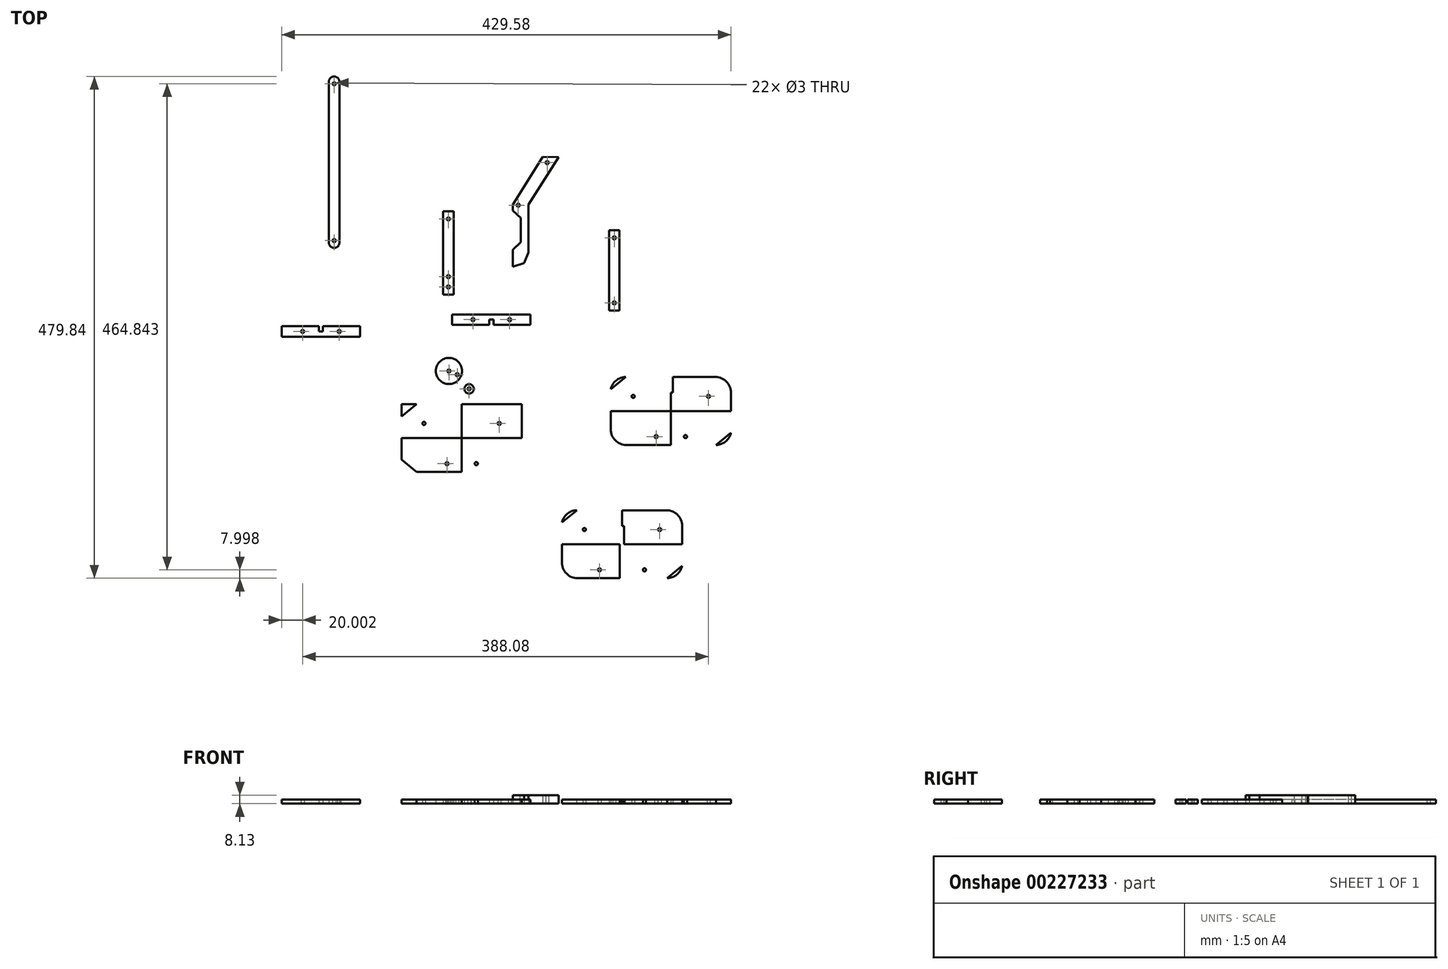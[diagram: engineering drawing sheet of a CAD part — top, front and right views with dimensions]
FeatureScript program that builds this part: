
annotation { "Feature Type Name" : "Feature", "Feature Type Description" : "" }
export const myFeature = defineFeature(function(context is Context, id is Id, definition is map)
    precondition{}
    {
        {
            var Q0;
            Q0=qCreatedBy(makeId("Top.planeOp"),FACE);
            var sketch = newSketch(context, id + "F0", { "sketchPlane" : qUnion([Q0])});
            skLineSegment(sketch, "E0", {"start": v(0, 50.66) * mm, "end": v(0, 45.05) * mm});
            skLineSegment(sketch, "E1", {"start": v(10.8, -5.12) * mm, "end": v(15.08, 4.77) * mm});
            skLineSegment(sketch, "E2", {"start": v(15.08, 4.77) * mm, "end": v(15.08, 50.66) * mm});
            skLineSegment(sketch, "E3", {"start": v(0, -8.6) * mm, "end": v(10.8, -5.12) * mm});
            skLineSegment(sketch, "E4", {"start": v(0, 50.66) * mm, "end": v(28.73, 96.18) * mm});
            skLineSegment(sketch, "E5", {"start": v(15.08, 50.66) * mm, "end": v(43.73, 96.06) * mm});
            skLineSegment(sketch, "E6", {"start": v(43.73, 96.06) * mm, "end": v(28.73, 96.18) * mm});
            skLineSegment(sketch, "E7", {"start": v(25.34, 90.81) * mm, "end": v(40.42, 90.81) * mm});
            skCircle(sketch, "E8", {"center": v(32.88, 90.81) * mm, "radius": 1.5 * mm});
            skLineSegment(sketch, "E9", {"start": v(0, 50.05) * mm, "end": v(15.08, 50.05) * mm});
            skCircle(sketch, "E10", {"center": v(5.2, 50.05) * mm, "radius": 1.5 * mm});
            skLineSegment(sketch, "E11", {"start": v(0, 7.4) * mm, "end": v(0, -8.6) * mm});
            skLineSegment(sketch, "E12", {"start": v(0, 45.05) * mm, "end": v(7.77, 45.05) * mm});
            skLineSegment(sketch, "E13", {"start": v(7.77, 45.05) * mm, "end": v(7.77, 7.4) * mm});
            skLineSegment(sketch, "E14", {"start": v(7.77, 7.4) * mm, "end": v(0, 7.4) * mm});
            skLineSegment(sketch, "E15", {"start": v(7.77, 26.22) * mm, "end": v(-3.47, 26.22) * mm});
            skLineSegment(sketch, "E16", {"start": v(0, 45.05) * mm, "end": v(7.77, 37.82) * mm});
            skLineSegment(sketch, "E17.MirrorCS", {"start": v(0, 7.4) * mm, "end": v(7.77, 14.63) * mm});
            skSolve(sketch);
        }
        {
            var Q0;
            Q0=makeQuery(id+"F0.imprint","IMPRINT",FACE,{"disambiguationData":[TD([[makeQuery(id+"F0.imprint","IMPRINT",EDGE,{"derivedFrom":sQuery(id+"F0.wireOp",EDGE,"xkdn2cEw-GIe6-0bhZ-HK7p-8BZ6EKmmzaHg")}),-1.0]])]});
            var Q1;
            Q1=makeQuery(id+"F0.imprint","IMPRINT",FACE,{"disambiguationData":[TD([[makeQuery(id+"F0.imprint","IMPRINT",EDGE,{"derivedFrom":sQuery(id+"F0.wireOp",EDGE,"E0")}),1.0]])]});
            var Q2;
            {var subQ5=sQuery(id+"F0.wireOp",EDGE,"E6");Q2=makeQuery(id+"F0.imprint","IMPRINT",FACE,{"disambiguationData":[TD([[makeQuery(id+"F0.imprint","IMPRINT",EDGE,{"derivedFrom":subQ5}),1.0]])]});}
            var Q3;
            {var subQ8=sQuery(id+"F0.wireOp",EDGE,"YExFYflc-ZLWd-MDCy-k9qd-3KOZYN6Y7YQf");Q3=makeQuery(id+"F0.imprint","IMPRINT",FACE,{"disambiguationData":[TD([[makeQuery(id+"F0.imprint","IMPRINT",EDGE,{"derivedFrom":subQ8}),1.0]])]});}
            var Q4;
            {var subQ15=sQuery(id+"F0.wireOp",EDGE,"E1");Q4=makeQuery(id+"F0.imprint","IMPRINT",FACE,{"disambiguationData":[TD([[makeQuery(id+"F0.imprint","IMPRINT",EDGE,{"derivedFrom":subQ15}),1.0]])]});}
            var Q5;
            {var subQ0=sQuery(id+"F0.wireOp",EDGE,"X9um9Srh-HxDp-66OW-7rEK-KayJhXlhD1Sx");Q5=makeQuery(id+"F0.imprint","IMPRINT",FACE,{"disambiguationData":[TD([[makeQuery(id+"F0.imprint","IMPRINT",EDGE,{"derivedFrom":subQ0}),-1.0]])]});}
            var Q6;
            {var subQ0=sQuery(id+"F0.wireOp",EDGE,"I0A4r3CH-8MeB-Zr2p-VjG7-bgiyZAQsyFYi");Q6=makeQuery(id+"F0.imprint","IMPRINT",FACE,{"disambiguationData":[TD([[makeQuery(id+"F0.imprint","IMPRINT",EDGE,{"derivedFrom":subQ0}),-1.0]])]});}
            var Q7;
            {var subQ0=sQuery(id+"F0.wireOp",EDGE,"E12");Q7=makeQuery(id+"F0.imprint","IMPRINT",FACE,{"disambiguationData":[TD([[makeQuery(id+"F0.imprint","IMPRINT",EDGE,{"derivedFrom":subQ0}),-1.0]])]});}
            var Q8;
            {var subQ0=sQuery(id+"F0.wireOp",EDGE,"E14");Q8=makeQuery(id+"F0.imprint","IMPRINT",FACE,{"disambiguationData":[TD([[makeQuery(id+"F0.imprint","IMPRINT",EDGE,{"derivedFrom":subQ0}),-1.0]])]});}
            extrude(context, id + "F1", {"entities" : qUnion([Q0, Q1, Q2, Q3, Q4, Q5, Q6, Q7, Q8]), "depth" : 8.13 * mm});
        }
        {
            var Q0;
            Q0=qCreatedBy(makeId("Top.planeOp"),FACE);
            var sketch = newSketch(context, id + "F2", { "sketchPlane" : qUnion([Q0])});
            skLineSegment(sketch, "E18.bottom", {"start": v(-66.59, 44.42) * mm, "end": v(-56.59, 44.42) * mm});
            skLineSegment(sketch, "E18.top", {"start": v(-66.59, -35.58) * mm, "end": v(-56.59, -35.58) * mm});
            skLineSegment(sketch, "E18.left", {"start": v(-66.59, 44.42) * mm, "end": v(-66.59, -35.58) * mm});
            skLineSegment(sketch, "E18.right", {"start": v(-56.59, 44.42) * mm, "end": v(-56.59, -35.58) * mm});
            skCircle(sketch, "E19", {"center": v(-61.59, -28.08) * mm, "radius": 1.5 * mm});
            skPoint(sketch, "E19.centerSnap0", {"position": v(-61.59, -35.58) * mm});
            skCircle(sketch, "E20", {"center": v(-61.59, 36.92) * mm, "radius": 1.5 * mm});
            skPoint(sketch, "E20.centerSnap0", {"position": v(-61.59, 44.42) * mm});
            skLineSegment(sketch, "E21.bottom", {"start": v(-106.43, -140.09) * mm, "end": v(8.57, -140.09) * mm});
            skLineSegment(sketch, "E21.top", {"start": v(-106.43, -205.09) * mm, "end": v(8.57, -205.09) * mm});
            skLineSegment(sketch, "E21.left", {"start": v(-106.43, -140.09) * mm, "end": v(-106.43, -205.09) * mm});
            skLineSegment(sketch, "E21.right", {"start": v(8.57, -140.09) * mm, "end": v(8.57, -205.09) * mm});
            skCircle(sketch, "E22", {"center": v(-62.93, -197.09) * mm, "radius": 1.5 * mm});
            skCircle(sketch, "E23", {"center": v(-12.93, -158.59) * mm, "radius": 1.5 * mm});
            skCircle(sketch, "E24", {"center": v(-61.08, -108.47) * mm, "radius": 12.5 * mm});
            skCircle(sketch, "E25", {"center": v(-61.08, -108.47) * mm, "radius": 1.5 * mm});
            skCircle(sketch, "E26", {"center": v(-53.14, -111.96) * mm, "radius": 1.5 * mm});
            skLineSegment(sketch, "E27.bottom", {"start": v(92.03, 18.82) * mm, "end": v(102.03, 18.82) * mm});
            skLineSegment(sketch, "E27.top", {"start": v(92.03, -43.35) * mm, "end": v(102.03, -43.35) * mm});
            skLineSegment(sketch, "E27.left", {"start": v(92.03, 18.82) * mm, "end": v(92.03, -43.35) * mm});
            skLineSegment(sketch, "E27.right", {"start": v(102.03, 18.82) * mm, "end": v(102.03, -43.35) * mm});
            skCircle(sketch, "E28", {"center": v(97.03, -43.35) * mm, "radius": 1.5 * mm});
            skCircle(sketch, "E29", {"center": v(97.03, 18.82) * mm, "radius": 1.5 * mm});
            skLineSegment(sketch, "E30", {"start": v(92.03, 18.82) * mm, "end": v(92.03, 26.3) * mm});
            skLineSegment(sketch, "E31", {"start": v(92.03, 26.3) * mm, "end": v(102.03, 26.3) * mm});
            skLineSegment(sketch, "E32", {"start": v(102.03, 26.3) * mm, "end": v(102.03, 18.82) * mm});
            skLineSegment(sketch, "E33", {"start": v(92.03, -43.35) * mm, "end": v(92.03, -50.57) * mm});
            skLineSegment(sketch, "E34", {"start": v(92.03, -50.57) * mm, "end": v(102.03, -50.57) * mm});
            skLineSegment(sketch, "E35", {"start": v(102.03, -50.57) * mm, "end": v(102.03, -43.35) * mm});
            skCircle(sketch, "E36", {"center": v(-41.76, -125.54) * mm, "radius": 4.5 * mm});
            skCircle(sketch, "E37", {"center": v(-41.76, -125.54) * mm, "radius": 1.5 * mm});
            skLineSegment(sketch, "E38", {"start": v(-48.93, -205.09) * mm, "end": v(-48.93, -140.09) * mm});
            skCircle(sketch, "E39.MirrorC", {"center": v(-84.93, -158.59) * mm, "radius": 1.5 * mm});
            skCircle(sketch, "E40.MirrorC", {"center": v(-34.93, -197.09) * mm, "radius": 1.5 * mm});
            skLineSegment(sketch, "E41", {"start": v(-106.43, -151.83) * mm, "end": v(-92.1, -140.09) * mm});
            skLineSegment(sketch, "E42", {"start": v(-106.43, -172.59) * mm, "end": v(8.57, -172.59) * mm});
            skLineSegment(sketch, "E43.MirrorCS", {"start": v(8.57, -151.83) * mm, "end": v(-5.75, -140.09) * mm});
            skLineSegment(sketch, "E44.MirrorCS", {"start": v(8.57, -193.35) * mm, "end": v(-5.75, -205.09) * mm});
            skLineSegment(sketch, "E45.MirrorCS", {"start": v(-106.43, -193.35) * mm, "end": v(-92.1, -205.09) * mm});
            skLineSegment(sketch, "E46", {"start": v(-66.59, -18.19) * mm, "end": v(-56.59, -18.19) * mm});
            skCircle(sketch, "E47", {"center": v(-61.59, -18.19) * mm, "radius": 1.5 * mm});
            skLineSegment(sketch, "E48.bottom", {"start": v(-58.07, -54.39) * mm, "end": v(16.93, -54.39) * mm});
            skLineSegment(sketch, "E48.top", {"start": v(-58.07, -64.39) * mm, "end": v(16.93, -64.39) * mm});
            skLineSegment(sketch, "E48.left", {"start": v(-58.07, -54.39) * mm, "end": v(-58.07, -64.39) * mm});
            skLineSegment(sketch, "E48.right", {"start": v(16.93, -54.39) * mm, "end": v(16.93, -64.39) * mm});
            skLineSegment(sketch, "E49", {"start": v(-38.07, -54.39) * mm, "end": v(-38.07, -64.39) * mm});
            skLineSegment(sketch, "E50", {"start": v(-3.07, -54.39) * mm, "end": v(-3.07, -64.39) * mm});
            skCircle(sketch, "E51", {"center": v(-38.07, -59.39) * mm, "radius": 1.5 * mm});
            skCircle(sketch, "E52", {"center": v(-3.07, -59.39) * mm, "radius": 1.5 * mm});
            skLineSegment(sketch, "E53.bottom", {"start": v(-175.82, 166.2) * mm, "end": v(-165.82, 166.2) * mm});
            skLineSegment(sketch, "E53.top", {"start": v(-175.82, 16.2) * mm, "end": v(-165.82, 16.2) * mm});
            skLineSegment(sketch, "E53.left", {"start": v(-175.82, 166.2) * mm, "end": v(-175.82, 16.2) * mm});
            skLineSegment(sketch, "E53.right", {"start": v(-165.82, 166.2) * mm, "end": v(-165.82, 16.2) * mm});
            skCircle(sketch, "E54", {"center": v(-170.82, 166.2) * mm, "radius": 1.5 * mm});
            skCircle(sketch, "E55", {"center": v(-170.82, 16.2) * mm, "radius": 1.5 * mm});
            skLineSegment(sketch, "E56", {"start": v(-175.82, 166.2) * mm, "end": v(-175.82, 173.2) * mm});
            skLineSegment(sketch, "E57", {"start": v(-175.82, 173.2) * mm, "end": v(-165.82, 173.2) * mm});
            skLineSegment(sketch, "E58", {"start": v(-165.82, 173.2) * mm, "end": v(-165.82, 166.2) * mm});
            skLineSegment(sketch, "E59", {"start": v(-175.82, 16.2) * mm, "end": v(-175.82, 9.2) * mm});
            skLineSegment(sketch, "E60", {"start": v(-175.82, 9.2) * mm, "end": v(-165.82, 9.2) * mm});
            skLineSegment(sketch, "E61", {"start": v(-165.82, 9.2) * mm, "end": v(-165.82, 16.2) * mm});
            skLineSegment(sketch, "E62.bottom", {"start": v(93.6, -114.22) * mm, "end": v(208.6, -114.22) * mm});
            skLineSegment(sketch, "E62.top", {"start": v(93.6, -179.22) * mm, "end": v(208.6, -179.22) * mm});
            skLineSegment(sketch, "E62.left", {"start": v(93.6, -114.22) * mm, "end": v(93.6, -179.22) * mm});
            skLineSegment(sketch, "E62.right", {"start": v(208.6, -114.22) * mm, "end": v(208.6, -179.22) * mm});
            skCircle(sketch, "E63", {"center": v(137.1, -171.22) * mm, "radius": 1.5 * mm});
            skCircle(sketch, "E64", {"center": v(187.1, -132.72) * mm, "radius": 1.5 * mm});
            skLineSegment(sketch, "E65", {"start": v(151.1, -179.22) * mm, "end": v(151.1, -114.22) * mm});
            skCircle(sketch, "E66.MirrorC", {"center": v(115.1, -132.72) * mm, "radius": 1.5 * mm});
            skCircle(sketch, "E67.MirrorC", {"center": v(165.1, -171.22) * mm, "radius": 1.5 * mm});
            skLineSegment(sketch, "E68", {"start": v(93.6, -125.96) * mm, "end": v(107.91, -114.22) * mm});
            skLineSegment(sketch, "E69", {"start": v(93.6, -146.72) * mm, "end": v(208.6, -146.72) * mm});
            skLineSegment(sketch, "E70.MirrorCS", {"start": v(208.6, -125.96) * mm, "end": v(194.27, -114.22) * mm});
            skLineSegment(sketch, "E71.MirrorCS", {"start": v(208.6, -167.48) * mm, "end": v(194.27, -179.22) * mm});
            skLineSegment(sketch, "E72.MirrorCS", {"start": v(93.6, -167.48) * mm, "end": v(107.91, -179.22) * mm});
            skLineSegment(sketch, "E73.bottom", {"start": v(46.9, -241.64) * mm, "end": v(161.9, -241.64) * mm});
            skLineSegment(sketch, "E73.top", {"start": v(46.9, -306.64) * mm, "end": v(161.9, -306.64) * mm});
            skLineSegment(sketch, "E73.left", {"start": v(46.9, -241.64) * mm, "end": v(46.9, -306.64) * mm});
            skLineSegment(sketch, "E73.right", {"start": v(161.9, -241.64) * mm, "end": v(161.9, -306.64) * mm});
            skCircle(sketch, "E74", {"center": v(82.9, -298.64) * mm, "radius": 1.5 * mm});
            skCircle(sketch, "E75", {"center": v(140.4, -260.14) * mm, "radius": 1.5 * mm});
            skLineSegment(sketch, "E76", {"start": v(104.4, -306.64) * mm, "end": v(104.4, -241.64) * mm});
            skCircle(sketch, "E77.MirrorC", {"center": v(68.4, -260.14) * mm, "radius": 1.5 * mm});
            skCircle(sketch, "E78.MirrorC", {"center": v(125.9, -298.64) * mm, "radius": 1.5 * mm});
            skLineSegment(sketch, "E79", {"start": v(46.9, -253.38) * mm, "end": v(61.23, -241.64) * mm});
            skLineSegment(sketch, "E80", {"start": v(46.9, -274.14) * mm, "end": v(161.9, -274.14) * mm});
            skLineSegment(sketch, "E81.MirrorCS", {"start": v(161.9, -253.38) * mm, "end": v(147.58, -241.64) * mm});
            skLineSegment(sketch, "E82.MirrorCS", {"start": v(161.9, -294.9) * mm, "end": v(147.58, -306.64) * mm});
            skLineSegment(sketch, "E83.MirrorCS", {"start": v(46.9, -294.9) * mm, "end": v(61.23, -306.64) * mm});
            skLineSegment(sketch, "E84", {"start": v(149.06, -114.22) * mm, "end": v(149.06, -129.22) * mm});
            skLineSegment(sketch, "E85", {"start": v(149.06, -129.22) * mm, "end": v(151.1, -129.22) * mm});
            skLineSegment(sketch, "E86.MirrorCS", {"start": v(153.12, -114.22) * mm, "end": v(153.12, -129.22) * mm});
            skLineSegment(sketch, "E87.MirrorCS", {"start": v(153.12, -129.22) * mm, "end": v(151.1, -129.22) * mm});
            skLineSegment(sketch, "E88", {"start": v(102.37, -306.64) * mm, "end": v(102.37, -256.64) * mm});
            skLineSegment(sketch, "E89", {"start": v(102.37, -256.64) * mm, "end": v(104.4, -256.64) * mm});
            skLineSegment(sketch, "E90.MirrorCS", {"start": v(106.44, -256.64) * mm, "end": v(104.4, -256.64) * mm});
            skLineSegment(sketch, "E91.MirrorCS", {"start": v(106.44, -306.64) * mm, "end": v(106.44, -256.64) * mm});
            skLineSegment(sketch, "E92.bottom", {"start": v(-220.99, -65.64) * mm, "end": v(-145.99, -65.64) * mm});
            skLineSegment(sketch, "E92.top", {"start": v(-220.99, -75.64) * mm, "end": v(-145.99, -75.64) * mm});
            skLineSegment(sketch, "E92.left", {"start": v(-220.99, -65.64) * mm, "end": v(-220.99, -75.64) * mm});
            skLineSegment(sketch, "E92.right", {"start": v(-145.99, -65.64) * mm, "end": v(-145.99, -75.64) * mm});
            skLineSegment(sketch, "E93", {"start": v(-200.99, -65.64) * mm, "end": v(-200.99, -75.64) * mm});
            skLineSegment(sketch, "E94", {"start": v(-165.99, -65.64) * mm, "end": v(-165.99, -75.64) * mm});
            skCircle(sketch, "E95", {"center": v(-200.99, -70.64) * mm, "radius": 1.5 * mm});
            skCircle(sketch, "E96", {"center": v(-165.99, -70.64) * mm, "radius": 1.5 * mm});
            skLineSegment(sketch, "E97", {"start": v(-183.49, -65.64) * mm, "end": v(-183.49, -75.64) * mm});
            skLineSegment(sketch, "E98", {"start": v(-185.52, -65.64) * mm, "end": v(-185.52, -70.64) * mm});
            skLineSegment(sketch, "E99", {"start": v(-185.52, -70.64) * mm, "end": v(-183.49, -70.64) * mm});
            skLineSegment(sketch, "E100.MirrorCS", {"start": v(-181.46, -65.64) * mm, "end": v(-181.46, -70.64) * mm});
            skLineSegment(sketch, "E101.MirrorCS", {"start": v(-181.46, -70.64) * mm, "end": v(-183.49, -70.64) * mm});
            skLineSegment(sketch, "E102", {"start": v(-20.57, -64.39) * mm, "end": v(-20.57, -54.39) * mm});
            skLineSegment(sketch, "E103", {"start": v(-22.6, -64.39) * mm, "end": v(-22.6, -59.39) * mm});
            skLineSegment(sketch, "E104", {"start": v(-22.6, -59.39) * mm, "end": v(-20.57, -59.39) * mm});
            skLineSegment(sketch, "E105.MirrorCS", {"start": v(-18.54, -59.39) * mm, "end": v(-20.57, -59.39) * mm});
            skLineSegment(sketch, "E106.MirrorCS", {"start": v(-18.54, -64.39) * mm, "end": v(-18.54, -59.39) * mm});
            skSolve(sketch);
        }
        {
            var Q0;
            {var subQ3=sQuery(id+"F2.wireOp",EDGE,"E41");Q0=makeQuery(id+"F2.imprint","IMPRINT",FACE,{"disambiguationData":[TD([[makeQuery(id+"F2.imprint","IMPRINT",EDGE,{"derivedFrom":subQ3}),1.0]])]});}
            var Q1;
            Q1=makeQuery(id+"F2.imprint","IMPRINT",FACE,{"disambiguationData":[TD([[makeQuery(id+"F2.imprint","IMPRINT",EDGE,{"derivedFrom":sQuery(id+"F2.wireOp",EDGE,"E18.bottom")}),-1.0]])]});
            var Q2;
            {var subQ3=sQuery(id+"F2.wireOp",EDGE,"E43.MirrorCS");Q2=makeQuery(id+"F2.imprint","IMPRINT",FACE,{"disambiguationData":[TD([[makeQuery(id+"F2.imprint","IMPRINT",EDGE,{"derivedFrom":subQ3}),-1.0]])]});}
            var Q3;
            Q3=makeQuery(id+"F2.imprint","IMPRINT",FACE,{"disambiguationData":[TD([[makeQuery(id+"F2.imprint","IMPRINT",EDGE,{"derivedFrom":sQuery(id+"F2.wireOp",EDGE,"E24")}),1.0]])]});
            var Q4;
            {var subQ4=sQuery(id+"F2.wireOp",EDGE,"E27.left");Q4=makeQuery(id+"F2.imprint","IMPRINT",FACE,{"disambiguationData":[TD([[makeQuery(id+"F2.imprint","IMPRINT",EDGE,{"derivedFrom":subQ4}),1.0]])]});}
            var Q5;
            {var subQ0=sQuery(id+"F2.wireOp",EDGE,"E30");Q5=makeQuery(id+"F2.imprint","IMPRINT",FACE,{"disambiguationData":[TD([[makeQuery(id+"F2.imprint","IMPRINT",EDGE,{"derivedFrom":subQ0}),-1.0]])]});}
            var Q6;
            {var subQ4=sQuery(id+"F2.wireOp",EDGE,"E33");Q6=makeQuery(id+"F2.imprint","IMPRINT",FACE,{"disambiguationData":[TD([[makeQuery(id+"F2.imprint","IMPRINT",EDGE,{"derivedFrom":subQ4}),1.0]])]});}
            var Q7;
            Q7=makeQuery(id+"F2.imprint","IMPRINT",FACE,{"disambiguationData":[TD([[makeQuery(id+"F2.imprint","IMPRINT",EDGE,{"derivedFrom":sQuery(id+"F2.wireOp",EDGE,"E36")}),1.0]])]});
            var Q8;
            Q8=makeQuery(id+"F2.imprint","IMPRINT",FACE,{"disambiguationData":[TD([[makeQuery(id+"F2.imprint","IMPRINT",EDGE,{"derivedFrom":sQuery(id+"F2.wireOp",EDGE,"E39.MirrorC")}),1.0]])]});
            var Q9;
            Q9=makeQuery(id+"F2.imprint","IMPRINT",FACE,{"disambiguationData":[TD([[makeQuery(id+"F2.imprint","IMPRINT",EDGE,{"derivedFrom":sQuery(id+"F2.wireOp",EDGE,"E22")}),-1.0]])]});
            var Q10;
            Q10=makeQuery(id+"F2.imprint","IMPRINT",FACE,{"disambiguationData":[TD([[makeQuery(id+"F2.imprint","IMPRINT",EDGE,{"derivedFrom":sQuery(id+"F2.wireOp",EDGE,"E23")}),-1.0]])]});
            var Q11;
            Q11=makeQuery(id+"F2.imprint","IMPRINT",FACE,{"disambiguationData":[TD([[makeQuery(id+"F2.imprint","IMPRINT",EDGE,{"derivedFrom":sQuery(id+"F2.wireOp",EDGE,"E40.MirrorC")}),1.0]])]});
            var Q12;
            {var subQ1=sQuery(id+"F2.wireOp",EDGE,"E18.top");Q12=makeQuery(id+"F2.imprint","IMPRINT",FACE,{"disambiguationData":[TD([[makeQuery(id+"F2.imprint","IMPRINT",EDGE,{"derivedFrom":subQ1}),1.0]])]});}
            var Q13;
            {var subQ0=sQuery(id+"F2.wireOp",EDGE,"E49");var subQ11=sQuery(id+"F2.wireOp",EDGE,"E48.bottom");var subQ12=makeQuery(id+"F2.imprint","INTERSECT",VERTEX,{"derivedFrom":[subQ11,subQ0]});Q13=makeQuery(id+"F2.imprint","IMPRINT",FACE,{"disambiguationData":[TD([[makeQuery(id+"F2.imprint","IMPRINT",EDGE,{"disambiguationData":[TD([[subQ12,-1.0]])],"derivedFrom":subQ11}),-1.0]])]});}
            var Q14;
            {var subQ0=sQuery(id+"F2.wireOp",EDGE,"E48.left");Q14=makeQuery(id+"F2.imprint","IMPRINT",FACE,{"disambiguationData":[TD([[makeQuery(id+"F2.imprint","IMPRINT",EDGE,{"derivedFrom":subQ0}),1.0]])]});}
            var Q15;
            {var subQ0=sQuery(id+"F2.wireOp",EDGE,"E48.right");Q15=makeQuery(id+"F2.imprint","IMPRINT",FACE,{"disambiguationData":[TD([[makeQuery(id+"F2.imprint","IMPRINT",EDGE,{"derivedFrom":subQ0}),-1.0]])]});}
            var Q16;
            {var subQ5=sQuery(id+"F2.wireOp",EDGE,"E53.left");Q16=makeQuery(id+"F2.imprint","IMPRINT",FACE,{"disambiguationData":[TD([[makeQuery(id+"F2.imprint","IMPRINT",EDGE,{"derivedFrom":subQ5}),1.0]])]});}
            var Q17;
            {var subQ5=sQuery(id+"F2.wireOp",EDGE,"E56");Q17=makeQuery(id+"F2.imprint","IMPRINT",FACE,{"disambiguationData":[TD([[makeQuery(id+"F2.imprint","IMPRINT",EDGE,{"derivedFrom":subQ5}),-1.0]])]});}
            var Q18;
            {var subQ0=sQuery(id+"F2.wireOp",EDGE,"E59");Q18=makeQuery(id+"F2.imprint","IMPRINT",FACE,{"disambiguationData":[TD([[makeQuery(id+"F2.imprint","IMPRINT",EDGE,{"derivedFrom":subQ0}),1.0]])]});}
            var Q19;
            Q19=makeQuery(id+"F2.imprint","IMPRINT",FACE,{"disambiguationData":[TD([[makeQuery(id+"F2.imprint","IMPRINT",EDGE,{"derivedFrom":sQuery(id+"F2.wireOp",EDGE,"E66.MirrorC")}),1.0]])]});
            var Q20;
            Q20=makeQuery(id+"F2.imprint","IMPRINT",FACE,{"disambiguationData":[TD([[makeQuery(id+"F2.imprint","IMPRINT",EDGE,{"derivedFrom":sQuery(id+"F2.wireOp",EDGE,"E63")}),-1.0]])]});
            var Q21;
            Q21=makeQuery(id+"F2.imprint","IMPRINT",FACE,{"disambiguationData":[TD([[makeQuery(id+"F2.imprint","IMPRINT",EDGE,{"derivedFrom":sQuery(id+"F2.wireOp",EDGE,"E67.MirrorC")}),1.0]])]});
            var Q22;
            Q22=makeQuery(id+"F2.imprint","IMPRINT",FACE,{"disambiguationData":[TD([[makeQuery(id+"F2.imprint","IMPRINT",EDGE,{"derivedFrom":sQuery(id+"F2.wireOp",EDGE,"E64")}),-1.0]])]});
            var Q23;
            {var subQ3=sQuery(id+"F2.wireOp",EDGE,"E70.MirrorCS");Q23=makeQuery(id+"F2.imprint","IMPRINT",FACE,{"disambiguationData":[TD([[makeQuery(id+"F2.imprint","IMPRINT",EDGE,{"derivedFrom":subQ3}),-1.0]])]});}
            var Q24;
            {var subQ3=sQuery(id+"F2.wireOp",EDGE,"E68");Q24=makeQuery(id+"F2.imprint","IMPRINT",FACE,{"disambiguationData":[TD([[makeQuery(id+"F2.imprint","IMPRINT",EDGE,{"derivedFrom":subQ3}),1.0]])]});}
            var Q25;
            {var subQ3=sQuery(id+"F2.wireOp",EDGE,"E72.MirrorCS");Q25=makeQuery(id+"F2.imprint","IMPRINT",FACE,{"disambiguationData":[TD([[makeQuery(id+"F2.imprint","IMPRINT",EDGE,{"derivedFrom":subQ3}),-1.0]])]});}
            var Q26;
            {var subQ3=sQuery(id+"F2.wireOp",EDGE,"E71.MirrorCS");Q26=makeQuery(id+"F2.imprint","IMPRINT",FACE,{"disambiguationData":[TD([[makeQuery(id+"F2.imprint","IMPRINT",EDGE,{"derivedFrom":subQ3}),1.0]])]});}
            var Q27;
            Q27=makeQuery(id+"F2.imprint","IMPRINT",FACE,{"disambiguationData":[TD([[makeQuery(id+"F2.imprint","IMPRINT",EDGE,{"derivedFrom":sQuery(id+"F2.wireOp",EDGE,"E78.MirrorC")}),1.0]])]});
            var Q28;
            Q28=makeQuery(id+"F2.imprint","IMPRINT",FACE,{"disambiguationData":[TD([[makeQuery(id+"F2.imprint","IMPRINT",EDGE,{"derivedFrom":sQuery(id+"F2.wireOp",EDGE,"E75")}),-1.0]])]});
            var Q29;
            {var subQ3=sQuery(id+"F2.wireOp",EDGE,"E81.MirrorCS");Q29=makeQuery(id+"F2.imprint","IMPRINT",FACE,{"disambiguationData":[TD([[makeQuery(id+"F2.imprint","IMPRINT",EDGE,{"derivedFrom":subQ3}),-1.0]])]});}
            var Q30;
            {var subQ3=sQuery(id+"F2.wireOp",EDGE,"E82.MirrorCS");Q30=makeQuery(id+"F2.imprint","IMPRINT",FACE,{"disambiguationData":[TD([[makeQuery(id+"F2.imprint","IMPRINT",EDGE,{"derivedFrom":subQ3}),1.0]])]});}
            var Q31;
            Q31=makeQuery(id+"F2.imprint","IMPRINT",FACE,{"disambiguationData":[TD([[makeQuery(id+"F2.imprint","IMPRINT",EDGE,{"derivedFrom":sQuery(id+"F2.wireOp",EDGE,"E74")}),-1.0]])]});
            var Q32;
            {var subQ3=sQuery(id+"F2.wireOp",EDGE,"E83.MirrorCS");Q32=makeQuery(id+"F2.imprint","IMPRINT",FACE,{"disambiguationData":[TD([[makeQuery(id+"F2.imprint","IMPRINT",EDGE,{"derivedFrom":subQ3}),-1.0]])]});}
            var Q33;
            Q33=makeQuery(id+"F2.imprint","IMPRINT",FACE,{"disambiguationData":[TD([[makeQuery(id+"F2.imprint","IMPRINT",EDGE,{"derivedFrom":sQuery(id+"F2.wireOp",EDGE,"E77.MirrorC")}),1.0]])]});
            var Q34;
            {var subQ3=sQuery(id+"F2.wireOp",EDGE,"E79");Q34=makeQuery(id+"F2.imprint","IMPRINT",FACE,{"disambiguationData":[TD([[makeQuery(id+"F2.imprint","IMPRINT",EDGE,{"derivedFrom":subQ3}),1.0]])]});}
            var Q35;
            {var subQ5=sQuery(id+"F2.wireOp",EDGE,"E92.left");Q35=makeQuery(id+"F2.imprint","IMPRINT",FACE,{"disambiguationData":[TD([[makeQuery(id+"F2.imprint","IMPRINT",EDGE,{"derivedFrom":subQ5}),1.0]])]});}
            var Q36;
            {var subQ9=sQuery(id+"F2.wireOp",EDGE,"E98");Q36=makeQuery(id+"F2.imprint","IMPRINT",FACE,{"disambiguationData":[TD([[makeQuery(id+"F2.imprint","IMPRINT",EDGE,{"derivedFrom":subQ9}),-1.0]])]});}
            var Q37;
            {var subQ8=sQuery(id+"F2.wireOp",EDGE,"E100.MirrorCS");Q37=makeQuery(id+"F2.imprint","IMPRINT",FACE,{"disambiguationData":[TD([[makeQuery(id+"F2.imprint","IMPRINT",EDGE,{"derivedFrom":subQ8}),1.0]])]});}
            var Q38;
            {var subQ0=sQuery(id+"F2.wireOp",EDGE,"E92.right");Q38=makeQuery(id+"F2.imprint","IMPRINT",FACE,{"disambiguationData":[TD([[makeQuery(id+"F2.imprint","IMPRINT",EDGE,{"derivedFrom":subQ0}),-1.0]])]});}
            var Q39;
            {var subQ11=sQuery(id+"F2.wireOp",EDGE,"E105.MirrorCS");Q39=makeQuery(id+"F2.imprint","IMPRINT",FACE,{"disambiguationData":[TD([[makeQuery(id+"F2.imprint","IMPRINT",EDGE,{"derivedFrom":subQ11}),-1.0]])]});}
            extrude(context, id + "F3", {"entities" : qUnion([Q0, Q1, Q2, Q3, Q4, Q5, Q6, Q7, Q8, Q9, Q10, Q11, Q12, Q13, Q14, Q15, Q16, Q17, Q18, Q19, Q20, Q21, Q22, Q23, Q24, Q25, Q26, Q27, Q28, Q29, Q30, Q31, Q32, Q33, Q34, Q35, Q36, Q37, Q38, Q39]), "depth" : 4.06 * mm});
        }
        {
            var Q0;
            Q0=makeQuery(id+"F3.opExtrude","SWEPT_EDGE",EDGE,{"disambiguationData":[OSD([sQuery(id+"F2.wireOp",EDGE,"E60"),sQuery(id+"F2.wireOp",EDGE,"E61")])]});
            var Q1;
            Q1=makeQuery(id+"F3.opExtrude","SWEPT_EDGE",EDGE,{"disambiguationData":[OSD([sQuery(id+"F2.wireOp",EDGE,"E59"),sQuery(id+"F2.wireOp",EDGE,"E60")])]});
            fillet(context, id + "F4", {"entities" : qUnion([Q0, Q1]), "radius" : 5 * mm, "tangentPropagation" : true, "allowEdgeOverflow" : false});
        }
        {
            var Q0;
            Q0=makeQuery(id+"F3.opExtrude","SWEPT_EDGE",EDGE,{"disambiguationData":[OSD([sQuery(id+"F2.wireOp",EDGE,"E57"),sQuery(id+"F2.wireOp",EDGE,"E58")])]});
            var Q1;
            Q1=makeQuery(id+"F3.opExtrude","SWEPT_EDGE",EDGE,{"disambiguationData":[OSD([sQuery(id+"F2.wireOp",EDGE,"E56"),sQuery(id+"F2.wireOp",EDGE,"E57")])]});
            fillet(context, id + "F5", {"entities" : qUnion([Q0, Q1]), "radius" : 5 * mm, "tangentPropagation" : true, "allowEdgeOverflow" : false});
        }
        {
            var Q0;
            Q0=makeQuery(id+"F3.opExtrude","SWEPT_EDGE",EDGE,{"disambiguationData":[OSD([sQuery(id+"F2.wireOp",EDGE,"E73.bottom"),sQuery(id+"F2.wireOp",EDGE,"E73.left")])]});
            var Q1;
            Q1=makeQuery(id+"F3.opExtrude","SWEPT_EDGE",EDGE,{"disambiguationData":[OSD([sQuery(id+"F2.wireOp",EDGE,"E73.top"),sQuery(id+"F2.wireOp",EDGE,"E73.left")])]});
            var Q2;
            Q2=makeQuery(id+"F3.opExtrude","SWEPT_EDGE",EDGE,{"disambiguationData":[OSD([sQuery(id+"F2.wireOp",EDGE,"E73.bottom"),sQuery(id+"F2.wireOp",EDGE,"E73.right")])]});
            var Q3;
            Q3=makeQuery(id+"F3.opExtrude","SWEPT_EDGE",EDGE,{"disambiguationData":[OSD([sQuery(id+"F2.wireOp",EDGE,"E73.top"),sQuery(id+"F2.wireOp",EDGE,"E73.right")])]});
            fillet(context, id + "F6", {"entities" : qUnion([Q0, Q1, Q2, Q3]), "radius" : 15 * mm, "tangentPropagation" : true, "allowEdgeOverflow" : false});
        }
        {
            var Q0;
            Q0=makeQuery(id+"F3.opExtrude","SWEPT_EDGE",EDGE,{"disambiguationData":[OSD([sQuery(id+"F2.wireOp",EDGE,"E62.top"),sQuery(id+"F2.wireOp",EDGE,"E62.left")])]});
            var Q1;
            Q1=makeQuery(id+"F3.opExtrude","SWEPT_EDGE",EDGE,{"disambiguationData":[OSD([sQuery(id+"F2.wireOp",EDGE,"E62.top"),sQuery(id+"F2.wireOp",EDGE,"E62.right")])]});
            var Q2;
            Q2=makeQuery(id+"F3.opExtrude","SWEPT_EDGE",EDGE,{"disambiguationData":[OSD([sQuery(id+"F2.wireOp",EDGE,"E62.bottom"),sQuery(id+"F2.wireOp",EDGE,"E62.right")])]});
            var Q3;
            Q3=makeQuery(id+"F3.opExtrude","SWEPT_EDGE",EDGE,{"disambiguationData":[OSD([sQuery(id+"F2.wireOp",EDGE,"E62.bottom"),sQuery(id+"F2.wireOp",EDGE,"E62.left")])]});
            fillet(context, id + "F7", {"entities" : qUnion([Q0, Q1, Q2, Q3]), "radius" : 15 * mm, "tangentPropagation" : true, "allowEdgeOverflow" : false});
        }
    });
